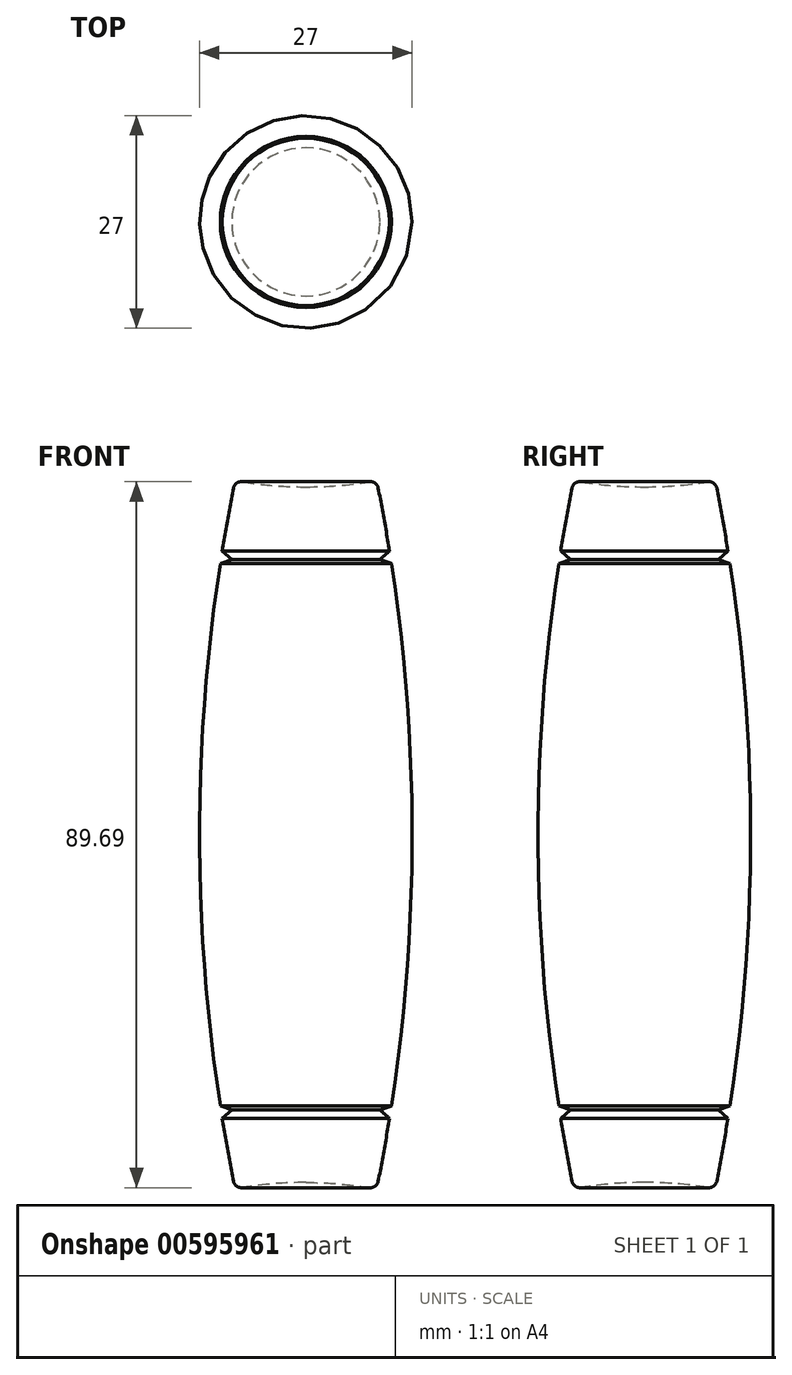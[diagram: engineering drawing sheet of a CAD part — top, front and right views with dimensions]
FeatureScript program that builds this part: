
annotation { "Feature Type Name" : "Feature", "Feature Type Description" : "" }
export const myFeature = defineFeature(function(context is Context, id is Id, definition is map)
    precondition{}
    {
        {
            var Q0;
            Q0=qCreatedBy(makeId("Front.planeOp"),FACE);
            var sketch = newSketch(context, id + "F0", { "sketchPlane" : qUnion([Q0])});
            skLineSegment(sketch, "E0", {"start": v(0, 0) * mm, "end": v(0, 88.37) * mm, "construction": true});
            skArc(sketch, "E1", {"start": v(9, -0.82) * mm, "mid": v(13.5, 44.18) * mm, "end": v(9, 89.18) * mm});
            skLineSegment(sketch, "E2", {"start": v(-213.5, 44.18) * mm, "end": v(0, 44.18) * mm, "construction": true});
            skLineSegment(sketch, "E3", {"start": v(13.5, 44.18) * mm, "end": v(13.5, 17.37) * mm, "construction": true});
            skLineSegment(sketch, "E4", {"start": v(0, 0) * mm, "end": v(0, 88.37) * mm});
            skArc(sketch, "E5", {"start": v(0, 88.37) * mm, "mid": v(4.52, 88.57) * mm, "end": v(9, 89.18) * mm});
            skLineSegment(sketch, "E6", {"start": v(9, 89.18) * mm, "end": v(-10.02, 89.18) * mm, "construction": true});
            skArc(sketch, "E7.MirrorCS", {"start": v(0, 0) * mm, "mid": v(4.52, -0.2) * mm, "end": v(9, -0.82) * mm});
            skLineSegment(sketch, "E8", {"start": v(9, -0.82) * mm, "end": v(-18, -0.82) * mm, "construction": true});
            skLineSegment(sketch, "E9", {"start": v(0, 88.37) * mm, "end": v(34.96, 88.37) * mm, "construction": true});
            skLineSegment(sketch, "E10", {"start": v(0, 0) * mm, "end": v(28.63, -0.2) * mm, "construction": true});
            skPoint(sketch, "E10.endSnap0", {"position": v(4.52, -0.2) * mm});
            skSolve(sketch);
        }
        {
            var Q0;
            Q0=makeQuery(id+"F0.imprint","IMPRINT",FACE,{"disambiguationData":[TD([[makeQuery(id+"F0.imprint","IMPRINT",EDGE,{"derivedFrom":sQuery(id+"F0.wireOp",EDGE,"E1")}),1.0]])]});
            var Q1;
            Q1=sQuery(id+"F0.wireOp",EDGE,"E4");
            revolve(context, id + "F1", {"entities" : qUnion([Q0]), "axis" : qUnion([Q1]), "revolveType" : RevolveType.FULL});
        }
        {
            var Q0;
            Q0=makeQuery(id+"F1.opRevolve","SWEPT_EDGE",EDGE,{"disambiguationData":[OSD([sQuery(id+"F0.wireOp",EDGE,"E1"),sQuery(id+"F0.wireOp",EDGE,"E5")])]});
            var Q1;
            Q1=makeQuery(id+"F1.opRevolve","SWEPT_EDGE",EDGE,{"disambiguationData":[OSD([sQuery(id+"F0.wireOp",EDGE,"E1"),sQuery(id+"F0.wireOp",EDGE,"E7.MirrorCS")])]});
            fillet(context, id + "F2", {"entities" : qUnion([Q0, Q1]), "radius" : 1 * mm, "tangentPropagation" : true, "allowEdgeOverflow" : false});
        }
        {
            var Q0;
            Q0=qCreatedBy(makeId("Front.planeOp"),FACE);
            var sketch = newSketch(context, id + "F3", { "sketchPlane" : qUnion([Q0])});
            skArc(sketch, "E11", {"start": v(-8.04, 89.02) * mm, "mid": v(0, 88.37) * mm, "end": v(8.04, 89.02) * mm, "construction": true});
            skArc(sketch, "E12", {"start": v(8.04, -0.65) * mm, "mid": v(0, 0) * mm, "end": v(-8.04, -0.65) * mm, "construction": true});
            skLineSegment(sketch, "E13", {"start": v(8.04, 89.02) * mm, "end": v(8.04, -0.65) * mm, "construction": true});
            skLineSegment(sketch, "E14", {"start": v(8.04, 44.18) * mm, "end": v(-31.5, 44.18) * mm, "construction": true});
            skLineSegment(sketch, "E15", {"start": v(14.73, 83.85) * mm, "end": v(9.4, 79.14) * mm});
            skLineSegment(sketch, "E16", {"start": v(9.4, 79.14) * mm, "end": v(17.61, 76.39) * mm});
            skLineSegment(sketch, "E17", {"start": v(14.73, 83.85) * mm, "end": v(17.61, 76.39) * mm});
            skLineSegment(sketch, "E18.MirrorCS", {"start": v(14.73, 4.52) * mm, "end": v(9.4, 9.23) * mm});
            skLineSegment(sketch, "E19.MirrorCS", {"start": v(9.4, 9.23) * mm, "end": v(17.61, 11.98) * mm});
            skLineSegment(sketch, "E20.MirrorCS", {"start": v(14.73, 4.52) * mm, "end": v(17.61, 11.98) * mm});
            skLineSegment(sketch, "E21", {"start": v(0, 0) * mm, "end": v(0, 55.62) * mm, "construction": true});
            skSolve(sketch);
        }
        {
            var Q0;
            Q0=qSketchRegion(id+"F3",true);
            var Q1;
            Q1=sQuery(id+"F3.wireOp",EDGE,"E21");
            revolve(context, id + "F4", {"operationType" : NewBodyOperationType.REMOVE, "entities" : qUnion([Q0]), "axis" : qUnion([Q1]), "revolveType" : RevolveType.FULL, "oppositeDirection" : true});
        }
    });
